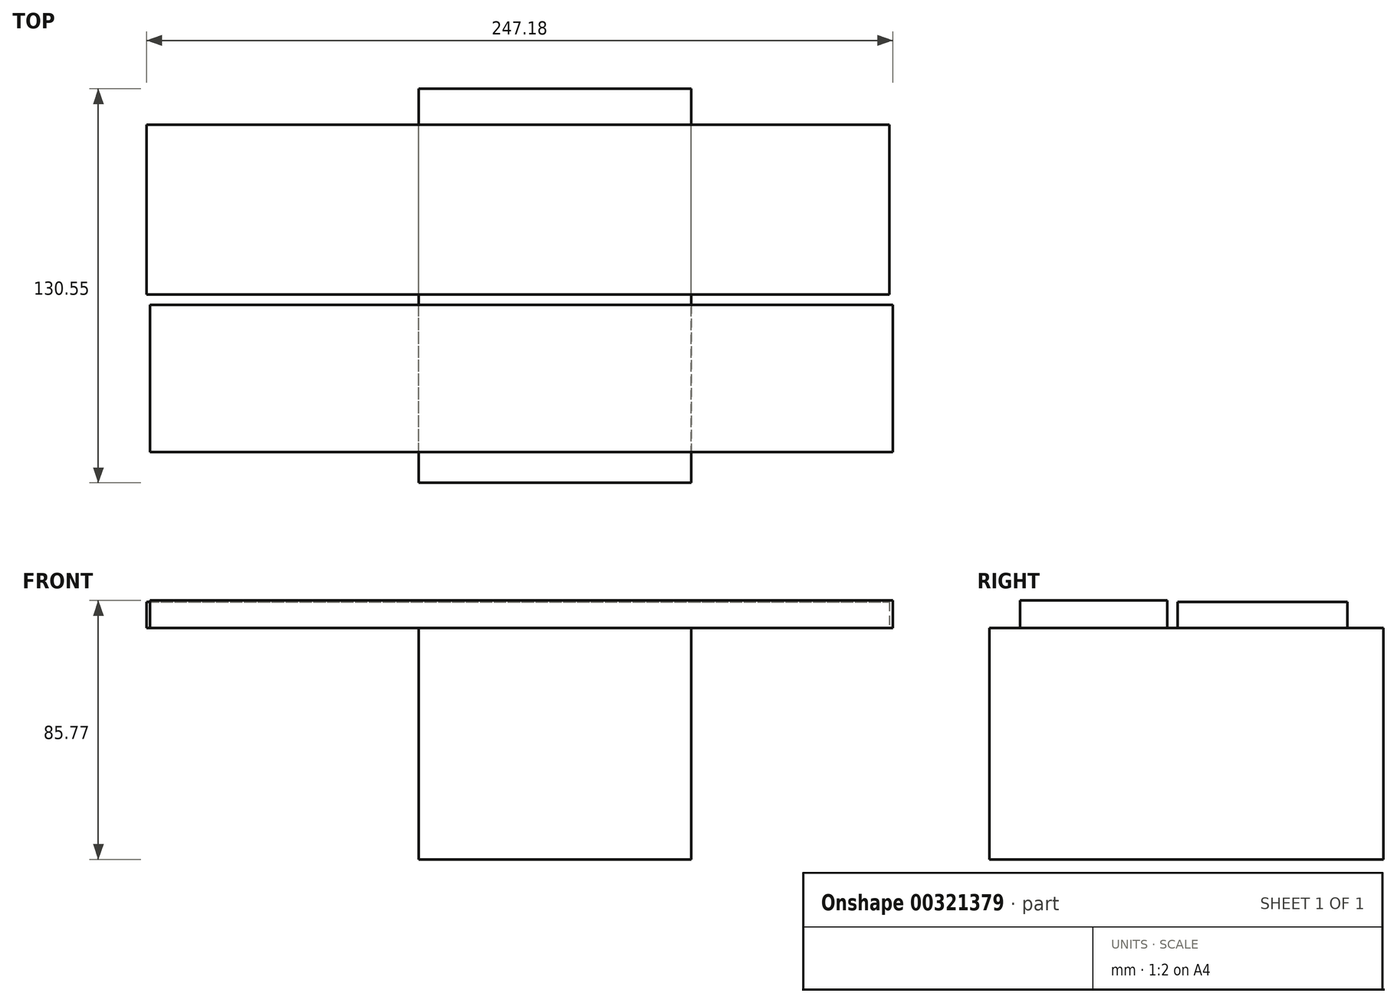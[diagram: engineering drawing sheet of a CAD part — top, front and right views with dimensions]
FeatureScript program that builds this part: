
annotation { "Feature Type Name" : "Feature", "Feature Type Description" : "" }
export const myFeature = defineFeature(function(context is Context, id is Id, definition is map)
    precondition{}
    {
        {
            var Q0;
            Q0=qCreatedBy(makeId("Front.planeOp"),FACE);
            var sketch = newSketch(context, id + "F0", { "sketchPlane" : qUnion([Q0])});
            skLineSegment(sketch, "E0.bottom", {"start": v(-42.17, 31.37) * mm, "end": v(48.08, 31.37) * mm});
            skLineSegment(sketch, "E0.top", {"start": v(-42.17, -45.26) * mm, "end": v(48.08, -45.26) * mm});
            skLineSegment(sketch, "E0.left", {"start": v(-42.17, 31.37) * mm, "end": v(-42.17, -45.26) * mm});
            skLineSegment(sketch, "E0.right", {"start": v(48.08, 31.37) * mm, "end": v(48.08, -45.26) * mm});
            skSolve(sketch);
        }
        {
            var Q0;
            Q0=makeQuery(id+"F0.imprint","IMPRINT",FACE,{"disambiguationData":[TD([[makeQuery(id+"F0.imprint","IMPRINT",EDGE,{"derivedFrom":sQuery(id+"F0.wireOp",EDGE,"E0.bottom")}),-1.0]])]});
            extrude(context, id + "F1", {"entities" : qUnion([Q0]), "depth" : 75.18 * mm});
        }
        {
            var Q0;
            Q0=makeQuery(id+"F1.opExtrude","SWEPT_FACE",FACE,{"disambiguationData":[OSD([sQuery(id+"F0.wireOp",EDGE,"E0.bottom")])]});
            var sketch = newSketch(context, id + "F2", { "sketchPlane" : qUnion([Q0])});
            skLineSegment(sketch, "E1.bottom", {"start": v(137, -16.17) * mm, "end": v(-39.2, -16.17) * mm});
            skLineSegment(sketch, "E1.top", {"start": v(137, -64.96) * mm, "end": v(-39.2, -64.96) * mm});
            skLineSegment(sketch, "E1.left", {"start": v(137, -64.96) * mm, "end": v(137, -16.17) * mm});
            skLineSegment(sketch, "E1.right", {"start": v(-39.2, -64.96) * mm, "end": v(-39.2, -16.17) * mm});
            skSolve(sketch);
        }
        {
            var Q0;
            {var subQ0=sQuery(id+"F2.wireOp",EDGE,"E1.right");Q0=makeQuery(id+"F2.imprint","IMPRINT",FACE,{"disambiguationData":[TD([[makeQuery(id+"F2.imprint","IMPRINT",EDGE,{"derivedFrom":subQ0}),-1.0]])]});}
            extrude(context, id + "F3", {"entities" : qUnion([Q0]), "operationType" : NewBodyOperationType.ADD, "depth" : 9.14 * mm});
        }
        {
            var Q0;
            {var subQ0=sQuery(id+"F0.wireOp",EDGE,"E0.right");Q0=makeQuery(id+"F3.boolean.opBoolean","MERGE",FACE,{"derivedFrom":[makeQuery(id+"F1.opExtrude","SWEPT_FACE",FACE,{"disambiguationData":[OSD([subQ0])]}),makeQuery(id+"F3.opExtrude","SWEPT_FACE",FACE,{"disambiguationData":[OSD([sQuery(id+"F0.wireOp",EDGE,"E0.bottom"),subQ0])]})]});}
            var sketch = newSketch(context, id + "F4", { "sketchPlane" : qUnion([Q0])});
            skLineSegment(sketch, "E2.bottom", {"start": v(-16.17, 31.37) * mm, "end": v(-64.96, 31.37) * mm});
            skLineSegment(sketch, "E2.top", {"start": v(-16.17, 40.51) * mm, "end": v(-64.96, 40.51) * mm});
            skLineSegment(sketch, "E2.left", {"start": v(-16.17, 31.37) * mm, "end": v(-16.17, 40.51) * mm});
            skLineSegment(sketch, "E2.right", {"start": v(-64.96, 31.37) * mm, "end": v(-64.96, 40.51) * mm});
            skSolve(sketch);
        }
        {
            var Q0;
            Q0=makeQuery(id+"F4.imprint","IMPRINT",FACE,{"disambiguationData":[TD([[makeQuery(id+"F4.imprint","IMPRINT",EDGE,{"derivedFrom":sQuery(id+"F4.wireOp",EDGE,"E2.bottom")}),-1.0]])]});
            extrude(context, id + "F5", {"entities" : qUnion([Q0]), "operationType" : NewBodyOperationType.ADD, "depth" : 66.8 * mm});
        }
        {
            var Q0;
            Q0=makeQuery(id+"F3.opExtrude","SWEPT_FACE",FACE,{"disambiguationData":[OSD([sQuery(id+"F2.wireOp",EDGE,"E1.right")])]});
            var sketch = newSketch(context, id + "F6", { "sketchPlane" : qUnion([Q0])});
            skSolve(sketch);
        }
        {
            var Q0;
            {var subQ0=sQuery(id+"F2.wireOp",EDGE,"E1.right");Q0=makeQuery(id+"F6.imprint","IMPRINT",FACE,{"disambiguationData":[TD([[makeQuery(id+"F6.imprint","IMPRINT",EDGE,{"derivedFrom":makeQuery(id+"F3.opExtrude","CAP_EDGE",EDGE,{"disambiguationData":[OSD([subQ0])],"isStart":false})}),1.0]])]});}
            extrude(context, id + "F7", {"entities" : qUnion([Q0]), "operationType" : NewBodyOperationType.ADD, "depth" : 91.95 * mm});
        }
        {
            var Q0;
            {var subQ0=sQuery(id+"F2.wireOp",EDGE,"E1.bottom");var subQ3=sQuery(id+"F0.wireOp",EDGE,"E0.bottom");Q0=makeQuery(id+"F7.boolean.opBoolean","SPLIT",FACE,{"disambiguationData":[TD([makeQuery(id+"F3.opExtrude","SWEPT_FACE",FACE,{"disambiguationData":[OSD([subQ0])]})])],"derivedFrom":makeQuery(id+"F1.opExtrude","SWEPT_FACE",FACE,{"disambiguationData":[OSD([subQ3])]})});}
            var sketch = newSketch(context, id + "F8", { "sketchPlane" : qUnion([Q0])});
            skLineSegment(sketch, "E3.bottom", {"start": v(-132.29, -12.78) * mm, "end": v(113.74, -12.78) * mm});
            skLineSegment(sketch, "E3.top", {"start": v(-132.29, 43.48) * mm, "end": v(113.74, 43.48) * mm});
            skLineSegment(sketch, "E3.left", {"start": v(-132.29, -12.78) * mm, "end": v(-132.29, 43.48) * mm});
            skLineSegment(sketch, "E3.right", {"start": v(113.74, -12.78) * mm, "end": v(113.74, 43.48) * mm});
            skSolve(sketch);
        }
        {
            var Q0;
            Q0=makeQuery(id+"F8.imprint","IMPRINT",FACE,{"disambiguationData":[TD([[makeQuery(id+"F8.imprint","IMPRINT",EDGE,{"derivedFrom":sQuery(id+"F8.wireOp",EDGE,"E3.top")}),-1.0]])]});
            var Q1;
            {var subQ5=sQuery(id+"F0.wireOp",EDGE,"E0.bottom");var subQ14=makeQuery(id+"F1.opExtrude","CAP_EDGE",EDGE,{"disambiguationData":[OSD([subQ5])],"isStart":true});Q1=makeQuery(id+"F8.imprint","IMPRINT",FACE,{"disambiguationData":[TD([[makeQuery(id+"F8.imprint","IMPRINT",EDGE,{"derivedFrom":subQ14}),-1.0]])]});}
            extrude(context, id + "F9", {"entities" : qUnion([Q0, Q1]), "operationType" : NewBodyOperationType.ADD, "depth" : 8.64 * mm});
        }
        {
            var Q0;
            Q0=makeQuery(id+"F1.opExtrude","CAP_FACE",FACE,{"disambiguationData":[OSD([sQuery(id+"F0.wireOp",EDGE,"E0.bottom"),sQuery(id+"F0.wireOp",EDGE,"E0.top"),sQuery(id+"F0.wireOp",EDGE,"E0.left"),sQuery(id+"F0.wireOp",EDGE,"E0.right")])],"isStart":true});
            extrude(context, id + "F10", {"entities" : qUnion([Q0]), "operationType" : NewBodyOperationType.ADD, "depth" : 55.37 * mm});
        }
    });
